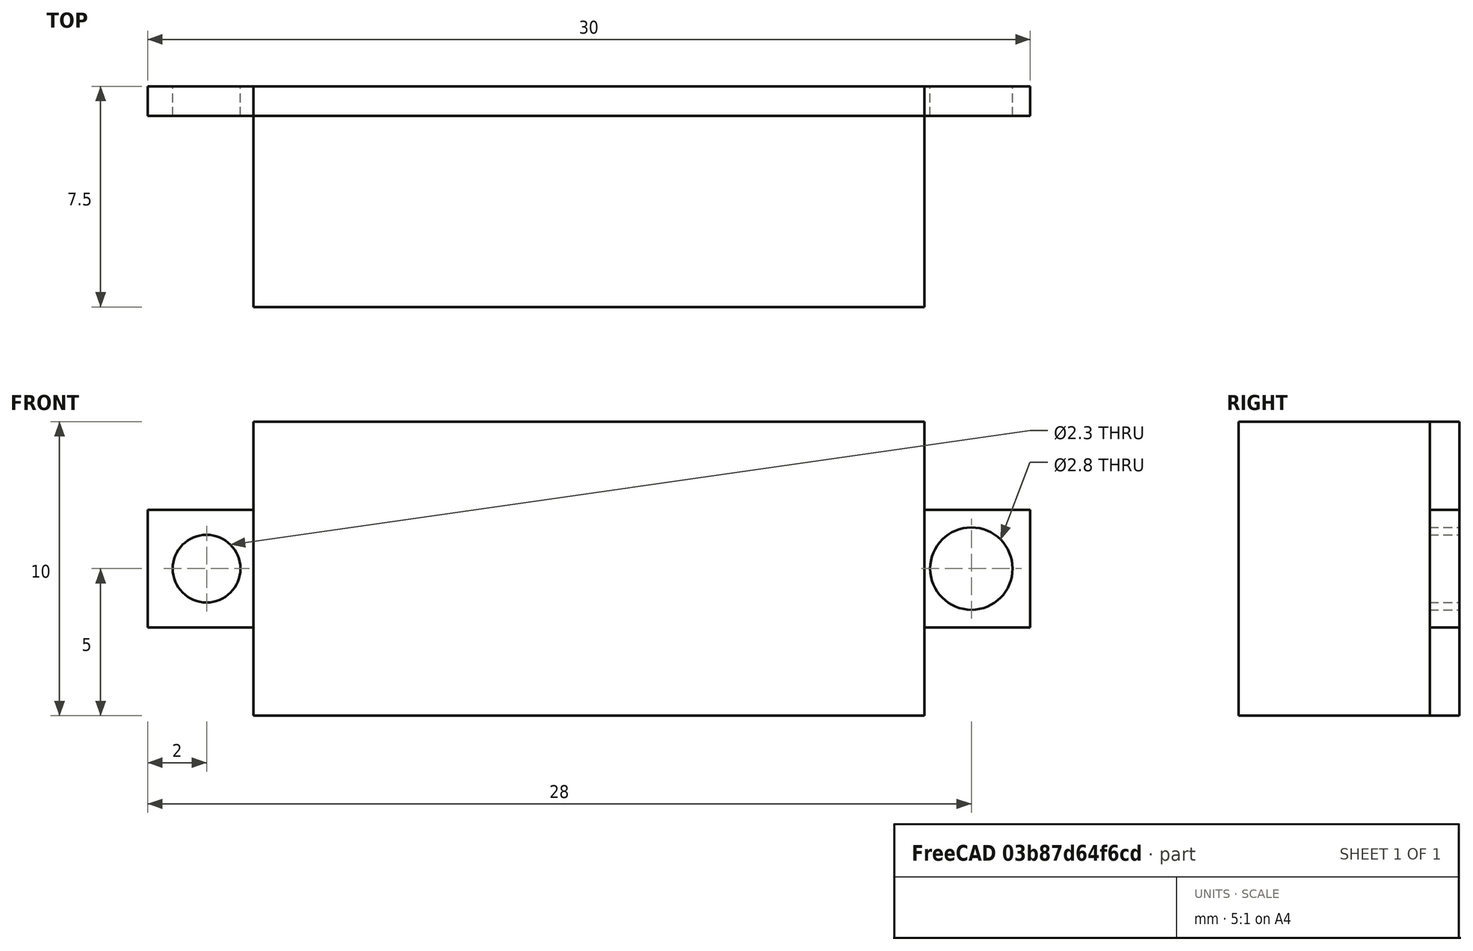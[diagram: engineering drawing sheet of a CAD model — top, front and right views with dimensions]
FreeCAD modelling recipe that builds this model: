
FCSTD DOCUMENT  (FreeCAD 0.19R24267 +148 (Git))
Label: 028voltm_003
License: All rights reserved
LicenseURL: http://en.wikipedia.org/wiki/All_rights_reserved
objects: Sketcher::SketchObject×1, PartDesign::Body×1, Part::Feature×1, Spreadsheet::Sheet×1, App::Part×1
note: 3 computed .brp shape members not serialized (recipe doc carries the construction recipe); baked Part::Feature solids carry a one-line shape summary decoded from their .brp

FEATURE [Sketcher::SketchObject] Sketch001
  FullyConstrained = true
  MapMode = 5
  Placement = pos=(0,0,0) rot=(1,0,0;1.5708rad)
  Support = -> [XZ_Plane001]
  sketch-geometry (7):
    g0: LineSegment StartX=-11.395 StartY=5.01 StartZ=0 EndX=11.395 EndY=5.01 EndZ=0
    g1: LineSegment StartX=11.395 StartY=5.01 StartZ=0 EndX=11.395 EndY=-5.01 EndZ=0
    g2: LineSegment StartX=11.395 StartY=-5.01 StartZ=0 EndX=-11.395 EndY=-5.01 EndZ=0
    g3: LineSegment StartX=-11.395 StartY=-5.01 StartZ=0 EndX=-11.395 EndY=5.01 EndZ=0
    g4: LineSegment StartX=-13.05 StartY=0 StartZ=0 EndX=13.05 EndY=0 EndZ=0
    g5: Circle CenterX=13.05 CenterY=0 CenterZ=0 NormalX=0 NormalY=0 NormalZ=1 AngleXU=0 Radius=1.15
    g6: Circle CenterX=-13.05 CenterY=0 CenterZ=0 NormalX=0 NormalY=0 NormalZ=1 AngleXU=0 Radius=1.15
  constraints (17):
    c: Coincident(g0,g1)
    c: Coincident(g1,g2)
    c: Coincident(g2,g3)
    c: Coincident(g3,g0)
    c: Horizontal(g2)
    c: Vertical(g1)
    c: PointOnObject(g4,g-1)
    c: DistanceY(g1,g1) = 10.02
    c: DistanceX(g4,g4) = 26.1
    c: DistanceX(g0,g0) = 22.79
    c: Coincident(g5,g4)
    c: Coincident(g6,g4)
    c: Equal(g6,g5)
    c: Diameter(g5) = 2.3
    c: Symmetric(g4,g4,g-2)
    c: Symmetric(g0,g2,g-1)
    c: Symmetric(g0,g0,g-2)
FEATURE [PartDesign::Body] Body
  Group = -> [Sketch001]
  Origin = -> Origin001
FEATURE [Part::Feature] Part__Feature003  label="LED DC Digital Voltmeter 5V Display grün"
  Placement = pos=(0,0,0) rot=(1,0,0;1.5708rad)
  shape: bbox 30 x 7.5 x 10 mm, 22 faces, 2 solids (baked)
FEATURE [Spreadsheet::Sheet] Spreadsheet  label="028voltmSp"
  cells = A2=larg; B2(larg)=10; A3=long; B3(long)=22.8; A4=haut; B4(haut)=6.6; A5=trouDiam; B5(trouDiam)=2.3; A6=trouEntraxe; B6(trouEntraxe)=26
FEATURE [App::Part] Part  label="028voltm"
  Group = -> [Body,Part__Feature003,Spreadsheet]
  Origin = -> Origin
